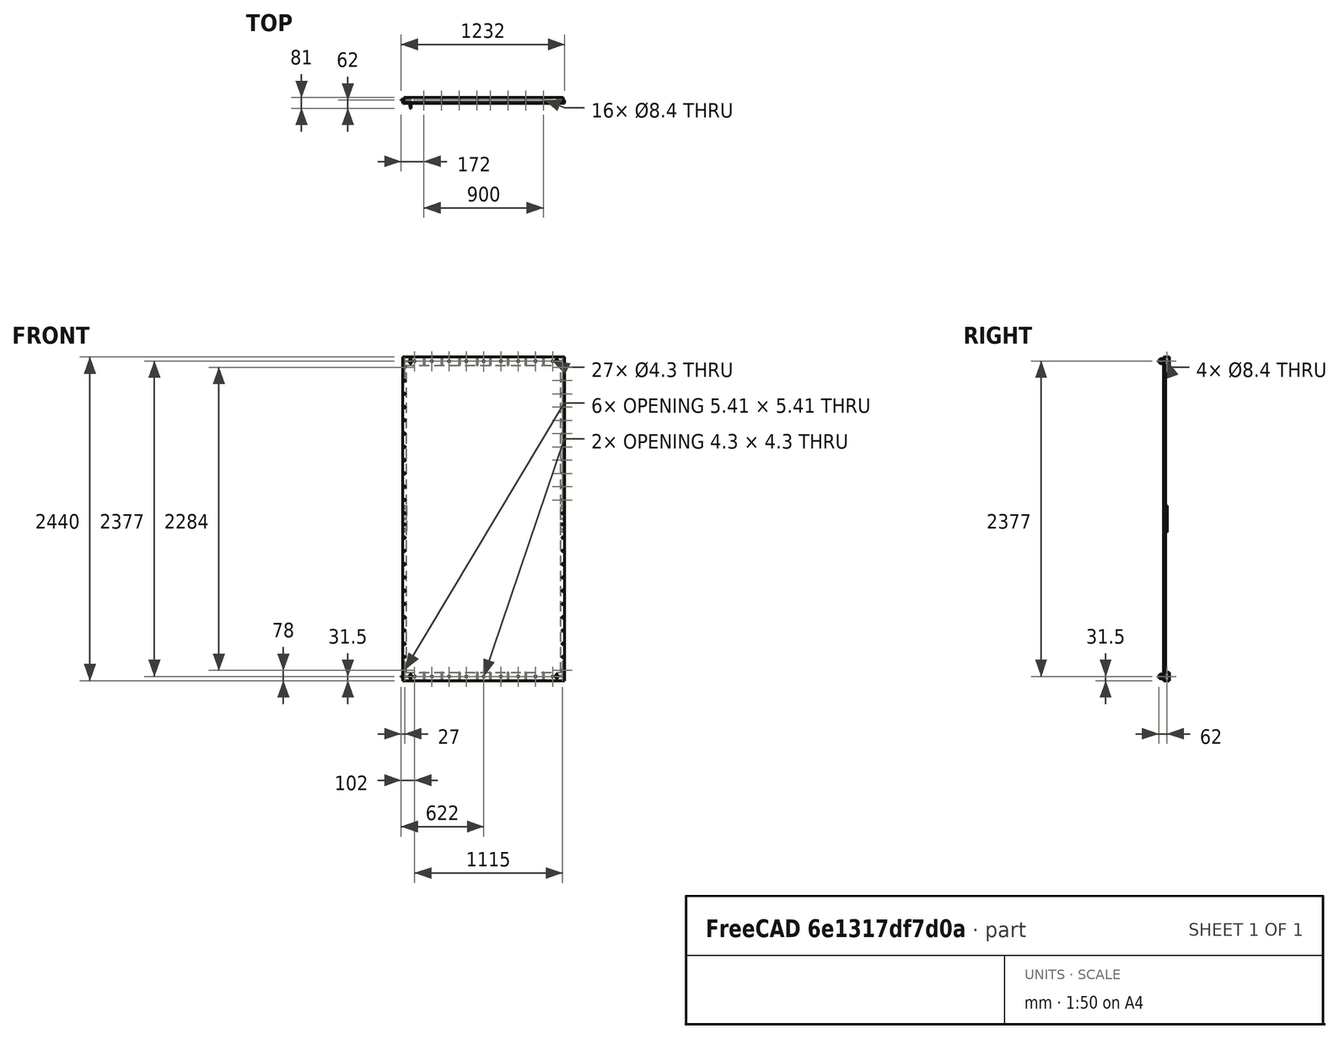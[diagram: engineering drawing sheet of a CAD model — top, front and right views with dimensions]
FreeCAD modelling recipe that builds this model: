
FCSTD DOCUMENT  (FreeCAD 0.21R33771 (Git))
Label: reflector_2024_assembly
License: All rights reserved
LicenseURL: https://en.wikipedia.org/wiki/All_rights_reserved
objects: Part::FeaturePython×28, Part::Compound×4, Part::Feature×4, TechDraw::DrawSVGTemplate×1, TechDraw::DrawPage×1, Part::Mirroring×1
note: 29 computed .brp shape members not serialized (recipe doc carries the construction recipe); baked Part::Feature solids carry a one-line shape summary decoded from their .brp

FEATURE [Part::FeaturePython] b_reflector_2024_panel_001_  label="reflector_2024_panel_panel_001"  # a2plus imported part (geometry in sourceFile) (typed FeaturePython)
  a2p_Version = 0.4.63
  fixedPosition = true
  objectType = a2pPart
  sourceFile = ./reflector_2024_panel.FCStd
  sourcePart = panel
  subassemblyImport = false
  timeLastImport = 1.70999e+09
  updateColors = true
FEATURE [Part::FeaturePython] b_reflector_2024_listello_001_  label="reflector_2024_listello_Body_001"  # a2plus imported part (geometry in sourceFile) (typed FeaturePython)
  Placement = pos=(-595,5,0) rot=(0,0,1;0rad)
  a2p_Version = 0.4.63
  fixedPosition = false
  objectType = a2pPart
  sourceFile = ./reflector_2024_listello.FCStd
  sourcePart = Body
  subassemblyImport = false
  timeLastImport = 1.70948e+09
  updateColors = true
  expr: .Placement.Base.x = -610 + 15
FEATURE [Part::FeaturePython] b_reflector_2024_listello_Body_001_  label="reflector_2024_listello_Body_002"  # a2plus imported part (geometry in sourceFile) (typed FeaturePython)
  Placement = pos=(595,5,0) rot=(0,-1,0;0rad)
  a2p_Version = 0.4.63
  fixedPosition = false
  objectType = a2pPart
  sourceFile = ./reflector_2024_listello.FCStd
  sourcePart = Body
  subassemblyImport = false
  timeLastImport = 1.70948e+09
  updateColors = true
  expr: .Placement.Base.x = 610 - 15
FEATURE [Part::FeaturePython] Screw006  label="M6x12-Screw"  # Fasteners workbench fastener (typed FeaturePython)
  Placement = pos=(595,-6,1142) rot=(1,0,0;1.5708rad)
  diameter = 8
  invert = false
  leftHanded = false
  length = 2
  lengthCustom = 12
  matchOuter = false
  offset = 0
  thread = false
  type = 73
  expr: .Placement.Base.x = 1220 / 2 - 30 / 2
  expr: .Placement.Base.y = -6
  expr: .Placement.Base.z = 1220 - 63 - 15
FEATURE [Part::FeaturePython] Array004  # Draft array (typed FeaturePython)
  AlwaysSyncPlacement = false
  Angle = 360
  ArrayType = 0
  Axis = (0,0,1)
  Base = -> Screw006
  Center = (0,0,0)
  Count = 12
  ExpandArray = false
  Fuse = false
  IntervalAxis = (0,0,0)
  IntervalX = (100,0,0)
  IntervalY = (0,100,0)
  IntervalZ = (0,0,-100)
  NumberCircles = 3
  NumberPolar = 5
  NumberX = 1
  NumberY = 1
  NumberZ = 12
  PlacementList = 12 placements: arithmetic series from (595,-6,1142) step (0,0,-100) to (595,-6,42)
  RadialDistance = 50
  ScaleList = (12) [(1,1,1),(1,1,1),(1,1,1),(1,1,1),(1,1,1),(1,1,1),(1,1,1),(1,1,1),(1,1,1),(1,1,1),(1,1,1),(1,1,1)]
  Symmetry = 1
  TangentialDistance = 25
FEATURE [Part::FeaturePython] Screw007  label="M6x12-Screw001"  # Fasteners workbench fastener (typed FeaturePython)
  Placement = pos=(595,-6,-1142) rot=(1,0,0;1.5708rad)
  diameter = 8
  invert = false
  leftHanded = false
  length = 2
  lengthCustom = 12
  matchOuter = false
  offset = 0
  thread = false
  type = 73
  expr: .Placement.Base.x = 1220 / 2 - 30 / 2
  expr: .Placement.Base.y = -6
  expr: .Placement.Base.z = -(1220 - 63 - 15)
FEATURE [Part::FeaturePython] Array005  # Draft array (typed FeaturePython)
  AlwaysSyncPlacement = false
  Angle = 360
  ArrayType = 0
  Axis = (0,0,1)
  Base = -> Screw007
  Center = (0,0,0)
  Count = 12
  ExpandArray = false
  Fuse = false
  IntervalAxis = (0,0,0)
  IntervalX = (100,0,0)
  IntervalY = (0,100,0)
  IntervalZ = (0,0,100)
  NumberCircles = 3
  NumberPolar = 5
  NumberX = 1
  NumberY = 1
  NumberZ = 12
  PlacementList = 12 placements: arithmetic series from (595,-6,-1142) step (0,0,100) to (595,-6,-42)
  RadialDistance = 50
  ScaleList = (12) [(1,1,1),(1,1,1),(1,1,1),(1,1,1),(1,1,1),(1,1,1),(1,1,1),(1,1,1),(1,1,1),(1,1,1),(1,1,1),(1,1,1)]
  Symmetry = 1
  TangentialDistance = 25
FEATURE [Part::FeaturePython] Screw008  label="M6x12-Screw004"  # Fasteners workbench fastener (typed FeaturePython)
  Placement = pos=(-595,-6,1142) rot=(1,0,0;1.5708rad)
  diameter = 8
  invert = false
  leftHanded = false
  length = 2
  lengthCustom = 12
  matchOuter = false
  offset = 0
  thread = false
  type = 73
  expr: .Placement.Base.x = -(1220 / 2 - 30 / 2)
  expr: .Placement.Base.y = -6
  expr: .Placement.Base.z = 1220 - 63 - 15
FEATURE [Part::FeaturePython] Array006  # Draft array (typed FeaturePython)
  AlwaysSyncPlacement = false
  Angle = 360
  ArrayType = 0
  Axis = (0,0,1)
  Base = -> Screw008
  Center = (0,0,0)
  Count = 12
  ExpandArray = false
  Fuse = false
  IntervalAxis = (0,0,0)
  IntervalX = (100,0,0)
  IntervalY = (0,100,0)
  IntervalZ = (0,0,-100)
  NumberCircles = 3
  NumberPolar = 5
  NumberX = 1
  NumberY = 1
  NumberZ = 12
  PlacementList = 12 placements: arithmetic series from (-595,-6,1142) step (0,0,-100) to (-595,-6,42)
  RadialDistance = 50
  ScaleList = (12) [(1,1,1),(1,1,1),(1,1,1),(1,1,1),(1,1,1),(1,1,1),(1,1,1),(1,1,1),(1,1,1),(1,1,1),(1,1,1),(1,1,1)]
  Symmetry = 1
  TangentialDistance = 25
FEATURE [Part::FeaturePython] Screw009  label="M6x12-Screw005"  # Fasteners workbench fastener (typed FeaturePython)
  Placement = pos=(-595,-6,-1142) rot=(1,0,0;1.5708rad)
  diameter = 8
  invert = false
  leftHanded = false
  length = 2
  lengthCustom = 12
  matchOuter = false
  offset = 0
  thread = false
  type = 73
  expr: .Placement.Base.x = -(1220 / 2 - 30 / 2)
  expr: .Placement.Base.y = -6
  expr: .Placement.Base.z = -(1220 - 63 - 15)
FEATURE [Part::FeaturePython] Array007  # Draft array (typed FeaturePython)
  AlwaysSyncPlacement = false
  Angle = 360
  ArrayType = 0
  Axis = (0,0,1)
  Base = -> Screw009
  Center = (0,0,0)
  Count = 12
  ExpandArray = false
  Fuse = false
  IntervalAxis = (0,0,0)
  IntervalX = (100,0,0)
  IntervalY = (0,100,0)
  IntervalZ = (0,0,100)
  NumberCircles = 3
  NumberPolar = 5
  NumberX = 1
  NumberY = 1
  NumberZ = 12
  PlacementList = 12 placements: arithmetic series from (-595,-6,-1142) step (0,0,100) to (-595,-6,-42)
  RadialDistance = 50
  ScaleList = (12) [(1,1,1),(1,1,1),(1,1,1),(1,1,1),(1,1,1),(1,1,1),(1,1,1),(1,1,1),(1,1,1),(1,1,1),(1,1,1),(1,1,1)]
  Symmetry = 1
  TangentialDistance = 25
FEATURE [Part::FeaturePython] Screw010  label="M6x8-Screw"  # Fasteners workbench fastener (typed FeaturePython)
  Placement = pos=(0,-6,1188.5) rot=(1,0,0;1.5708rad)
  diameter = 8
  invert = false
  leftHanded = false
  length = 0
  lengthCustom = 8
  matchOuter = false
  offset = 0
  thread = false
  type = 73
FEATURE [Part::FeaturePython] Array  # Draft array (typed FeaturePython)
  AlwaysSyncPlacement = false
  Angle = 360
  ArrayType = 0
  Axis = (0,0,1)
  Base = -> Screw010
  Center = (0,0,0)
  Count = 5
  ExpandArray = false
  Fuse = false
  IntervalAxis = (0,0,0)
  IntervalX = (130,0,0)
  IntervalY = (0,100,0)
  IntervalZ = (0,0,100)
  NumberCircles = 3
  NumberPolar = 5
  NumberX = 5
  NumberY = 1
  NumberZ = 1
  PlacementList = 5 placements: arithmetic series from (0,-6,1188.5) step (130,0,0) to (520,-6,1188.5)
  RadialDistance = 50
  ScaleList = (5) [(1,1,1),(1,1,1),(1,1,1),(1,1,1),(1,1,1)]
  Symmetry = 1
  TangentialDistance = 25
FEATURE [Part::Compound] Compound001  label="screws_listelli"
  Links = -> [Array004,Array005,Array006,Array007]
FEATURE [Part::FeaturePython] Array008  # Draft array (typed FeaturePython)
  AlwaysSyncPlacement = false
  Angle = 360
  ArrayType = 0
  Axis = (0,0,1)
  Base = -> Screw010
  Center = (0,0,0)
  Count = 5
  ExpandArray = false
  Fuse = false
  IntervalAxis = (0,0,0)
  IntervalX = (-130,0,0)
  IntervalY = (0,100,0)
  IntervalZ = (0,0,100)
  NumberCircles = 3
  NumberPolar = 5
  NumberX = 5
  NumberY = 1
  NumberZ = 1
  PlacementList = 5 placements: arithmetic series from (0,-6,1188.5) step (-130,0,0) to (-520,-6,1188.5)
  RadialDistance = 50
  ScaleList = (5) [(1,1,1),(1,1,1),(1,1,1),(1,1,1),(1,1,1)]
  Symmetry = 1
  TangentialDistance = 25
FEATURE [Part::FeaturePython] Screw011  label="M6x8-Screw001"  # Fasteners workbench fastener (typed FeaturePython)
  Placement = pos=(0,-6,-1188.5) rot=(1,0,0;1.5708rad)
  diameter = 8
  invert = false
  leftHanded = false
  length = 0
  lengthCustom = 8
  matchOuter = false
  offset = 0
  thread = false
  type = 73
  expr: .Placement.Base.z = -1188.5 mm
FEATURE [Part::FeaturePython] Array009  # Draft array (typed FeaturePython)
  AlwaysSyncPlacement = false
  Angle = 360
  ArrayType = 0
  Axis = (0,0,1)
  Base = -> Screw011
  Center = (0,0,0)
  Count = 5
  ExpandArray = false
  Fuse = false
  IntervalAxis = (0,0,0)
  IntervalX = (130,0,0)
  IntervalY = (0,100,0)
  IntervalZ = (0,0,100)
  NumberCircles = 3
  NumberPolar = 5
  NumberX = 5
  NumberY = 1
  NumberZ = 1
  PlacementList = 5 placements: arithmetic series from (0,-6,-1188.5) step (130,0,0) to (520,-6,-1188.5)
  RadialDistance = 50
  ScaleList = (5) [(1,1,1),(1,1,1),(1,1,1),(1,1,1),(1,1,1)]
  Symmetry = 1
  TangentialDistance = 25
FEATURE [Part::FeaturePython] Array010  # Draft array (typed FeaturePython)
  AlwaysSyncPlacement = false
  Angle = 360
  ArrayType = 0
  Axis = (0,0,1)
  Base = -> Screw011
  Center = (0,0,0)
  Count = 5
  ExpandArray = false
  Fuse = false
  IntervalAxis = (0,0,0)
  IntervalX = (-130,0,0)
  IntervalY = (0,100,0)
  IntervalZ = (0,0,100)
  NumberCircles = 3
  NumberPolar = 5
  NumberX = 5
  NumberY = 1
  NumberZ = 1
  PlacementList = 5 placements: arithmetic series from (0,-6,-1188.5) step (-130,0,0) to (-520,-6,-1188.5)
  RadialDistance = 50
  ScaleList = (5) [(1,1,1),(1,1,1),(1,1,1),(1,1,1),(1,1,1)]
  Symmetry = 1
  TangentialDistance = 25
FEATURE [Part::Compound] Compound  label="screws_battens"
  Links = -> [Array,Array008,Array009,Array010]
FEATURE [Part::Feature] Part__Feature  label="LIFTING EYE BOLT - M8 - DIN 580_1"
  Placement = pos=(550,-25,1188.5) rot=(0.707107,0,-0.707107;3.14159rad)
  shape: bbox 21.03 x 49.35 x 36.93 mm, 59 faces (baked)
  expr: .Placement.Base.x = 610 - 60
  expr: .Placement.Base.z = 1220 - 63 / 2
FEATURE [Part::Feature] Part__Feature001  label="LIFTING EYE BOLT - M8 - DIN 580_2"
  Placement = pos=(-550,-25,1188.5) rot=(0.707107,0,-0.707107;3.14159rad)
  shape: bbox 21.03 x 49.35 x 36.93 mm, 59 faces (baked)
  expr: .Placement.Base.x = -(610 - 60)
  expr: .Placement.Base.z = 1220 - 63 / 2
FEATURE [Part::Feature] Part__Feature002  label="LIFTING EYE BOLT - M8 - DIN 580_3"
  Placement = pos=(550,-25,-1188.5) rot=(0.707107,0,-0.707107;3.14159rad)
  shape: bbox 21.03 x 49.35 x 36.93 mm, 59 faces (baked)
  expr: .Placement.Base.x = 610 - 60
  expr: .Placement.Base.z = -(1220 - 63 / 2)
FEATURE [Part::Feature] Part__Feature003  label="LIFTING EYE BOLT - M8 - DIN 580_4"
  Placement = pos=(-550,-25,-1188.5) rot=(0.707107,0,-0.707107;3.14159rad)
  shape: bbox 21.03 x 49.35 x 36.93 mm, 59 faces (baked)
  expr: .Placement.Base.x = -(610 - 60)
  expr: .Placement.Base.z = -(1220 - 63 / 2)
FEATURE [Part::Compound] Compound002  label="eye_bolts"
  Links = -> [Part__Feature,Part__Feature001,Part__Feature002,Part__Feature003]
FEATURE [Part::FeaturePython] b_reflector_2024_listello_handle_001_  label="reflector_2024_listello_handle_001"  # a2plus imported part (geometry in sourceFile) (typed FeaturePython)
  Placement = pos=(595,20,0) rot=(0,0,1;0rad)
  a2p_Version = 0.4.63
  fixedPosition = false
  objectType = a2pPart
  sourceFile = ./reflector_2024_listello_handle.FCStd
  subassemblyImport = false
  timeLastImport = 1.70999e+09
  updateColors = true
  expr: .Placement.Base.x = 610 - 15
FEATURE [Part::FeaturePython] b_reflector_2024_listello_handle_001_001  label="reflector_2024_listello_handle_002"  # a2plus imported part (geometry in sourceFile) (typed FeaturePython)
  Placement = pos=(-595,20,0) rot=(0,0,1;0rad)
  a2p_Version = 0.4.63
  fixedPosition = false
  objectType = a2pPart
  sourceFile = ./reflector_2024_listello_handle.FCStd
  subassemblyImport = false
  timeLastImport = 1.70999e+09
  updateColors = true
  expr: .Placement.Base.x = -610 + 15
FEATURE [Part::FeaturePython] Screw  label="M6x8-Screw002"  # Fasteners workbench fastener (typed FeaturePython)
  Placement = pos=(595,21,0) rot=(-1,0,0;1.5708rad)
  diameter = 8
  invert = false
  leftHanded = false
  length = 0
  lengthCustom = 8
  matchOuter = false
  offset = 0
  thread = false
  type = 73
  expr: .Placement.Base.x = 610 - 15
FEATURE [Part::FeaturePython] Screw012  label="M6x8-Screw003"  # Fasteners workbench fastener (typed FeaturePython)
  Placement = pos=(595,21,80) rot=(-1,0,0;1.5708rad)
  diameter = 8
  invert = false
  leftHanded = false
  length = 0
  lengthCustom = 8
  matchOuter = false
  offset = 0
  thread = false
  type = 73
  expr: .Placement.Base.x = 610 - 15
FEATURE [Part::FeaturePython] Screw013  label="M6x8-Screw004"  # Fasteners workbench fastener (typed FeaturePython)
  Placement = pos=(595,21,-80) rot=(-1,0,0;1.5708rad)
  diameter = 8
  invert = false
  leftHanded = false
  length = 0
  lengthCustom = 8
  matchOuter = false
  offset = 0
  thread = false
  type = 73
  expr: .Placement.Base.x = 610 - 15
FEATURE [Part::FeaturePython] Screw014  label="M6x8-Screw008"  # Fasteners workbench fastener (typed FeaturePython)
  Placement = pos=(-595,21,0) rot=(-1,0,0;1.5708rad)
  diameter = 8
  invert = false
  leftHanded = false
  length = 0
  lengthCustom = 8
  matchOuter = false
  offset = 0
  thread = false
  type = 73
  expr: .Placement.Base.x = -610 + 15
FEATURE [Part::FeaturePython] Screw015  label="M6x8-Screw009"  # Fasteners workbench fastener (typed FeaturePython)
  Placement = pos=(-595,21,80) rot=(-1,0,0;1.5708rad)
  diameter = 8
  invert = false
  leftHanded = false
  length = 0
  lengthCustom = 8
  matchOuter = false
  offset = 0
  thread = false
  type = 73
  expr: .Placement.Base.x = -610 + 15
FEATURE [Part::FeaturePython] Screw016  label="M6x8-Screw010"  # Fasteners workbench fastener (typed FeaturePython)
  Placement = pos=(-595,21,-80) rot=(-1,0,0;1.5708rad)
  diameter = 8
  invert = false
  leftHanded = false
  length = 0
  lengthCustom = 8
  matchOuter = false
  offset = 0
  thread = false
  type = 73
  expr: .Placement.Base.x = -610 + 15
FEATURE [Part::Compound] Compound003  label="screws_handles"
  Links = -> [Screw,Screw012,Screw013,Screw014,Screw015,Screw016]
FEATURE [Part::FeaturePython] b_reflector_2024_timber_001_  label="reflector_2024_timber_001"  # a2plus imported part (geometry in sourceFile) (typed FeaturePython)
  Placement = pos=(0,19,1188.5) rot=(0,0,1;0rad)
  a2p_Version = 0.4.63
  fixedPosition = false
  objectType = a2pPart
  sourceFile = ./reflector_2024_timber.FCStd
  subassemblyImport = false
  timeLastImport = 1.71009e+09
  updateColors = true
  expr: .Placement.Base.y = 38 / 2
FEATURE [Part::FeaturePython] b_reflector_2024_timber_001_001  label="reflector_2024_timber_002"  # a2plus imported part (geometry in sourceFile) (typed FeaturePython)
  Placement = pos=(0,19,-1188.5) rot=(0,0,1;0rad)
  a2p_Version = 0.4.63
  fixedPosition = false
  objectType = a2pPart
  sourceFile = ./reflector_2024_timber.FCStd
  subassemblyImport = false
  timeLastImport = 1.71009e+09
  updateColors = true
  expr: .Placement.Base.y = 38 / 2
FEATURE [TechDraw::DrawSVGTemplate] Template
  Height = 594
  Orientation = 1
  Template = /snap/freecad/908/usr/share/Mod/TechDraw/Templates/A1_Landscape_blank.svg
  Width = 841
FEATURE [TechDraw::DrawPage] Page
  KeepUpdated = true
  NextBalloonIndex = 1
  ProjectionType = 0
  Template = -> Template
FEATURE [Part::FeaturePython] ScrewTap  label="M8x35-ScrewTap"  # Fasteners workbench fastener (typed FeaturePython)
  Placement = pos=(622,19,-1188.5) rot=(0,1,0;1.5708rad)
  diameter = 9
  diameterCustom = 6
  invert = false
  leftHanded = false
  length = 35
  matchOuter = false
  offset = 0
  pitchCustom = 1
  thread = false
  type = 2
  expr: .Placement.Base.y = 38 / 2
  expr: .Placement.Base.z = -1220 + 63 / 2
FEATURE [Part::Mirroring] Mirror  label="M8x35-ScrewTap (mirrored)"
  Base = (0,0,0)
  Normal = (1,0,0)
  Source = -> ScrewTap
